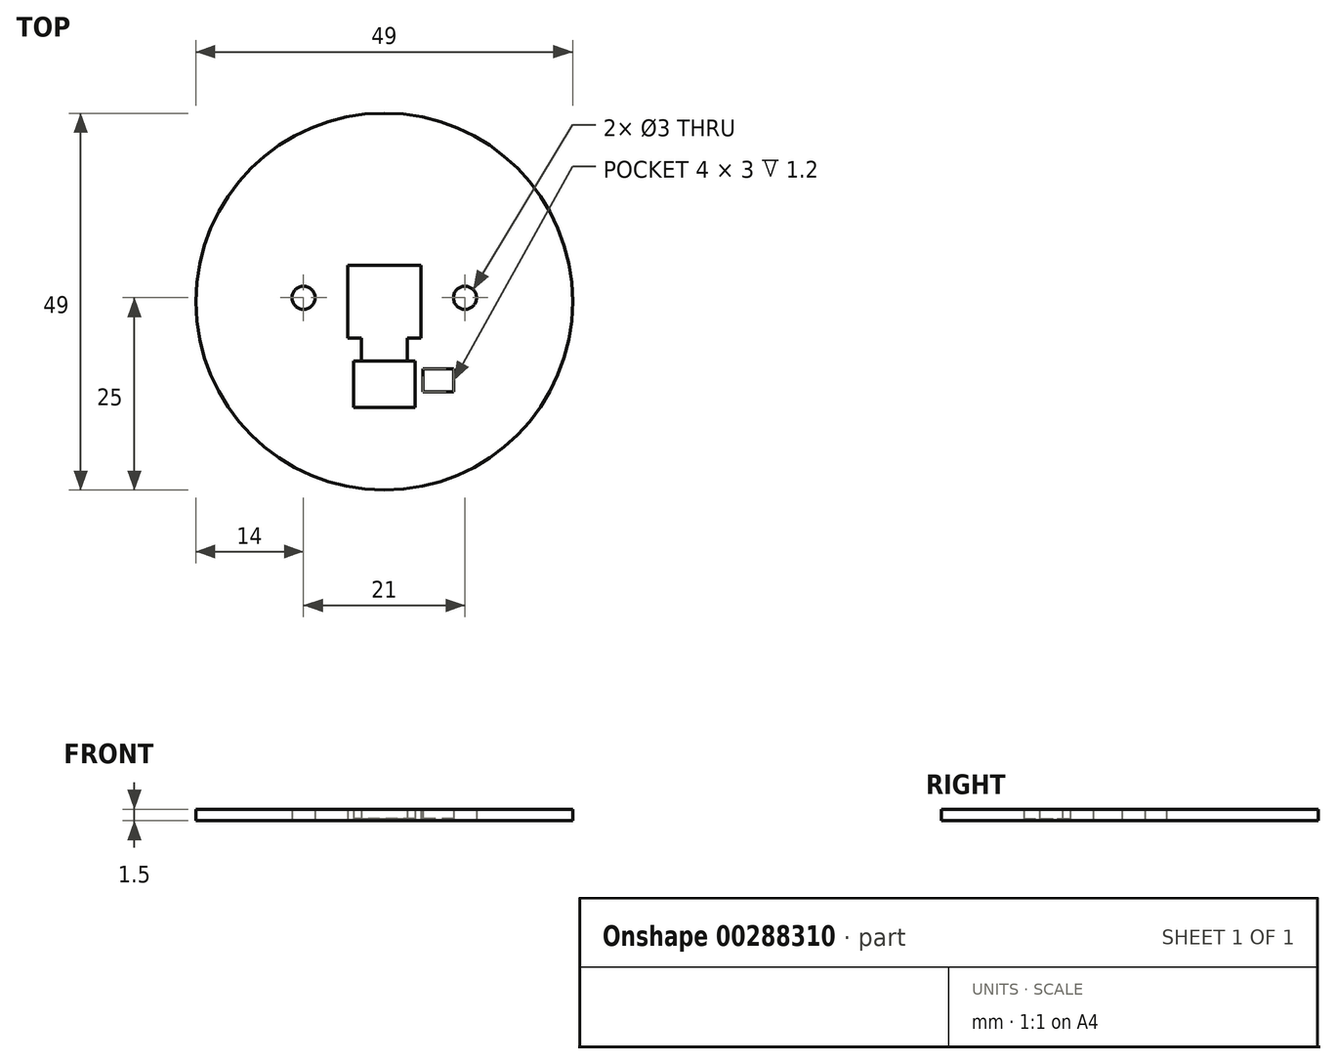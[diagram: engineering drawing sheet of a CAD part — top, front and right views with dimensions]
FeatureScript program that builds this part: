
annotation { "Feature Type Name" : "Feature", "Feature Type Description" : "" }
export const myFeature = defineFeature(function(context is Context, id is Id, definition is map)
    precondition{}
    {
        {
            var Q0;
            Q0=qCreatedBy(makeId("Top.planeOp"),FACE);
            var sketch = newSketch(context, id + "F0", { "sketchPlane" : qUnion([Q0])});
            skCircle(sketch, "E0", {"center": v(0, 0) * mm, "radius": 24.5 * mm});
            skPoint(sketch, "E1", {"position": v(-10.5, 0) * mm});
            skCircle(sketch, "E2", {"center": v(-10.5, 0.5) * mm, "radius": 1.5 * mm});
            skPoint(sketch, "E3", {"position": v(10.5, 0) * mm});
            skCircle(sketch, "E4", {"center": v(10.5, 0.5) * mm, "radius": 1.5 * mm});
            skLineSegment(sketch, "E5.bottom", {"start": v(-4.75, 4.75) * mm, "end": v(4.75, 4.75) * mm});
            skLineSegment(sketch, "E5.top", {"start": v(-4.75, -4.75) * mm, "end": v(4.75, -4.75) * mm});
            skLineSegment(sketch, "E5.left", {"start": v(-4.75, 4.75) * mm, "end": v(-4.75, -4.75) * mm});
            skLineSegment(sketch, "E5.right", {"start": v(4.75, 4.75) * mm, "end": v(4.75, -4.75) * mm});
            skLineSegment(sketch, "E6.bottom", {"start": v(-4, -7.75) * mm, "end": v(4, -7.75) * mm});
            skLineSegment(sketch, "E6.top", {"start": v(-4, -13.75) * mm, "end": v(4, -13.75) * mm});
            skLineSegment(sketch, "E6.left", {"start": v(-4, -7.75) * mm, "end": v(-4, -13.75) * mm});
            skLineSegment(sketch, "E6.right", {"start": v(4, -7.75) * mm, "end": v(4, -13.75) * mm});
            skLineSegment(sketch, "E7.bottom", {"start": v(-3, -4.75) * mm, "end": v(3, -4.75) * mm});
            skLineSegment(sketch, "E7.top", {"start": v(-3, -7.75) * mm, "end": v(3, -7.75) * mm});
            skLineSegment(sketch, "E7.left", {"start": v(-3, -4.75) * mm, "end": v(-3, -7.75) * mm});
            skLineSegment(sketch, "E7.right", {"start": v(3, -4.75) * mm, "end": v(3, -7.75) * mm});
            skLineSegment(sketch, "E8.bottom", {"start": v(5, -8.75) * mm, "end": v(9, -8.75) * mm});
            skLineSegment(sketch, "E8.top", {"start": v(5, -11.75) * mm, "end": v(9, -11.75) * mm});
            skLineSegment(sketch, "E8.left", {"start": v(5, -8.75) * mm, "end": v(5, -11.75) * mm});
            skLineSegment(sketch, "E8.right", {"start": v(9, -8.75) * mm, "end": v(9, -11.75) * mm});
            skSolve(sketch);
        }
        {
            var Q0;
            Q0=makeQuery(id+"F0.imprint","IMPRINT",FACE,{"disambiguationData":[TD([[makeQuery(id+"F0.imprint","IMPRINT",EDGE,{"derivedFrom":sQuery(id+"F0.wireOp",EDGE,"E0")}),1.0]])]});
            var Q1;
            Q1=makeQuery(id+"F0.imprint","IMPRINT",FACE,{"disambiguationData":[TD([[makeQuery(id+"F0.imprint","IMPRINT",EDGE,{"derivedFrom":sQuery(id+"F0.wireOp",EDGE,"E8.bottom")}),-1.0]])]});
            var Q2;
            Q2=makeQuery(id+"F0.imprint","IMPRINT",FACE,{"disambiguationData":[TD([[makeQuery(id+"F0.imprint","IMPRINT",EDGE,{"derivedFrom":sQuery(id+"F0.wireOp",EDGE,"E6.top")}),1.0]])]});
            var Q3;
            Q3=makeQuery(id+"F0.imprint","IMPRINT",FACE,{"disambiguationData":[TD([[makeQuery(id+"F0.imprint","IMPRINT",EDGE,{"derivedFrom":sQuery(id+"F0.wireOp",EDGE,"E7.bottom")}),-1.0]])]});
            extrude(context, id + "F1", {"entities" : qUnion([Q0, Q1, Q2, Q3]), "depth" : .3 * mm});
        }
        {
            var Q0;
            Q0 = qSketchRegion(id + "F0", true);
            extrude(context, id + "F2", {"entities" : qUnion([Q0]), "operationType" : NewBodyOperationType.ADD, "depth" : 1.5 * mm});
        }
    });
